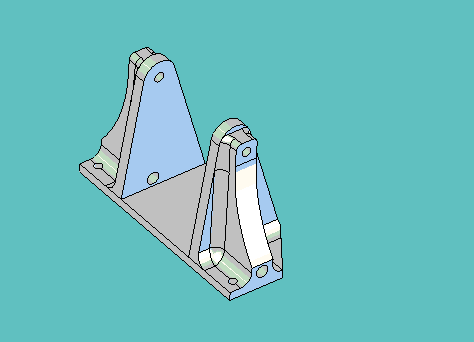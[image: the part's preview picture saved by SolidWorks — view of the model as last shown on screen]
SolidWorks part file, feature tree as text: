
SOLIDWORKS PART (.sldprt)
format: sldprt  version: not decoded by parser v0  size: 767,488 bytes
history: native  units: mm
features: sketch x9, extrude x5, cut_extrude x4, plane x2, fillet x2, material x1 (+11 scaffold rows collapsed)
feature tree (34):
  scaffold x11  (default folders/planes/origin — collapsed)
  material  "Material <not specified>"
  sketch  "Sketch2"  dims[c1.D7=9.525mm c1.D9=3.175mm c1.D1=2.3876mm c1.D2=27.94mm c1.D3=27.94mm c1.D4=~2.38125mm c1.D5=19.05mm c1.D6=19.05mm c1.D8=38.1mm c2.D5=19.05mm c2.D6=9.525mm c2.D3=9.525mm c2.D2=6.35mm c3.D5=15.875mm c3.D3=9.525mm c3.D6=~2.243212mm c3.D2=5.08mm c3.D4=5.08mm c4.D6=38.1mm]
  extrude  "Extrude1"  Depth=3.175mm
  plane  "Plane1"  Offset=27.0256mm
  sketch  "Sketch5"  dims[D1=0.0mm]
  extrude  "Extrude3"  Depth=3.175mm
  plane  "Plane2"  Offset=13.5128mm
  sketch  "Sketch7"
  extrude  "Extrude5"  [1 undecoded]
  sketch  "Sketch9"  dims[D1=30.1625mm D2=6.35mm]
  extrude  "Extrude6"  [1 undecoded]
  sketch  "Sketch10"  dims[c1.D1=6.35mm c1.D2=4.7625mm c1.D3=28.575mm c2.D2=4.7625mm c2.D3=36.5125mm c2.D4=6.35mm]
  extrude  "Extrude7"  Depth=3.175mm
  sketch  "Sketch8"  dims[D2=4.7625mm D1=4.7625mm]
  cut_extrude  "Cut-Extrude1"  Depth=6.35mm
  sketch  "Sketch13"
  cut_extrude  "Cut-Extrude4"  Depth=6.35mm
  sketch  "Sketch11"  dims[c1.D3=3.175mm c1.D2=~3.96875mm c1.D1=1.5875mm c2.D2=~8.41375mm c2.D3=~38.10635mm c2.D4=~36.51885mm c2.D1=38.1mm c3.D2=50.8mm]
  cut_extrude  "Cut-Extrude2"  [1 undecoded]
  sketch  "Sketch12"  dims[c1.D3=~2.778125mm c1.D4=~2.778125mm c1.D6=~2.778125mm c1.D7=~2.778125mm c1.D1=26.9875mm c1.D2=26.9875mm c1.D5=12.7mm c1.D8=11.43mm c1.D9=11.43mm c2.D5=6.35mm c2.D6=19.05mm]
  cut_extrude  "Cut-Extrude3"  [1 undecoded]
  fillet  "Fillet1"  Radius=2.54mm
  fillet  "Fillet2"  Radius=1.5875mm
decode coverage: 14 of 20 modeling features carry decoded parameters
note: ~ marks probable driven/reference dimensions
note: 4 parameter values undecoded
summary: no parameter record found for 4 features
note: suppression state not decoded; provenance and decode notes live in map.json
